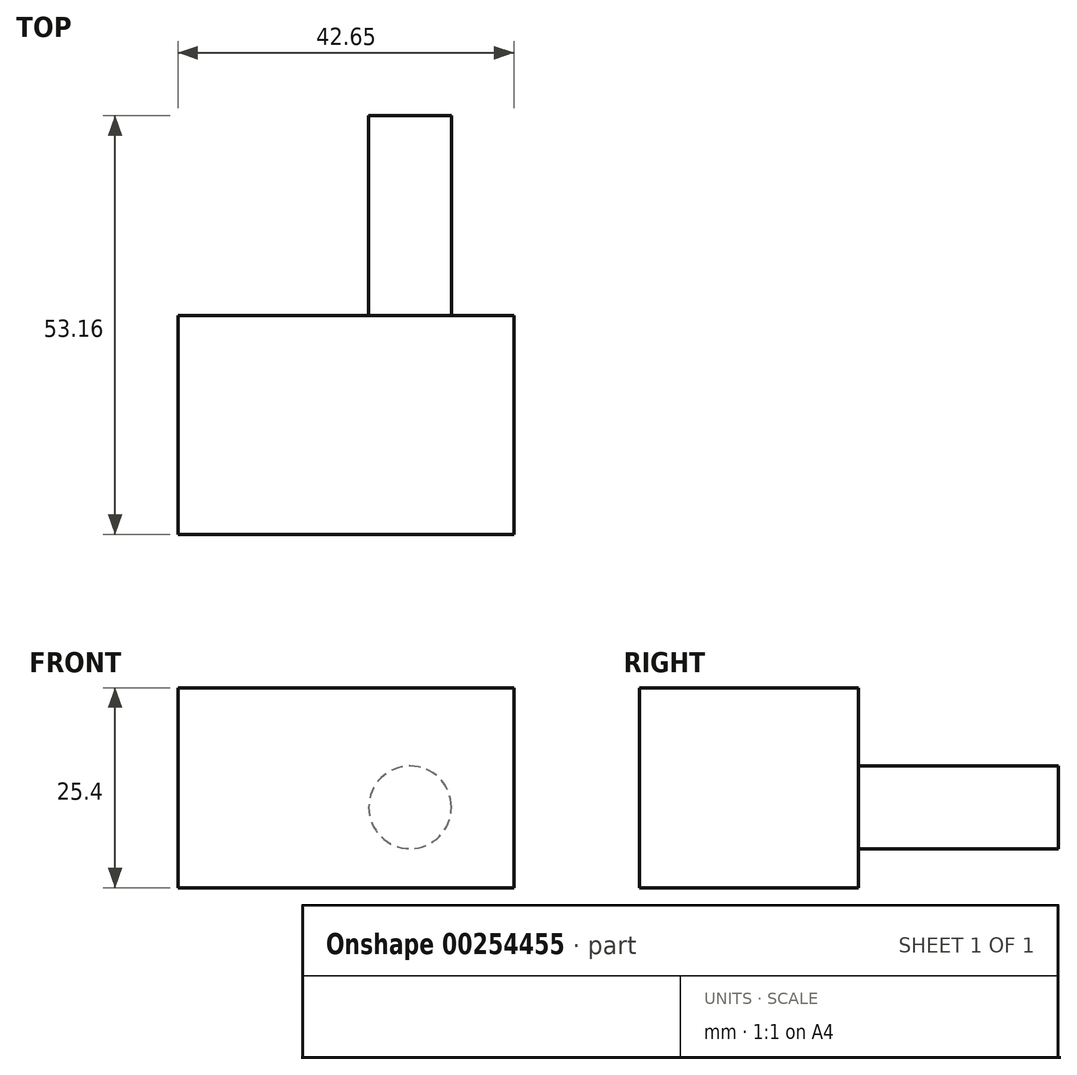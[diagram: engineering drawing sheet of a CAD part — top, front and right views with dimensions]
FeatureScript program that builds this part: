
annotation { "Feature Type Name" : "Feature", "Feature Type Description" : "" }
export const myFeature = defineFeature(function(context is Context, id is Id, definition is map)
    precondition{}
    {
        {
            var Q0;
            Q0=qCreatedBy(makeId("Top.planeOp"),FACE);
            var sketch = newSketch(context, id + "F0", { "sketchPlane" : qUnion([Q0])});
            skLineSegment(sketch, "E0.bottom", {"start": v(-68.58, 17.38) * mm, "end": v(-25.93, 17.38) * mm});
            skLineSegment(sketch, "E0.top", {"start": v(-68.58, -10.38) * mm, "end": v(-25.93, -10.38) * mm});
            skLineSegment(sketch, "E0.left", {"start": v(-68.58, 17.38) * mm, "end": v(-68.58, -10.38) * mm});
            skLineSegment(sketch, "E0.right", {"start": v(-25.93, 17.38) * mm, "end": v(-25.93, -10.38) * mm});
            skSolve(sketch);
        }
        {
            var Q0;
            Q0 = qSketchRegion(id + "F0", true);
            extrude(context, id + "F1", {"entities" : qUnion([Q0]), "depth" : 25.4 * mm});
        }
        {
            var Q0;
            Q0=makeQuery(id+"F1.opExtrude","SWEPT_FACE",FACE,{"disambiguationData":[OSD([sQuery(id+"F0.wireOp",EDGE,"E0.bottom")])]});
            var sketch = newSketch(context, id + "F2", { "sketchPlane" : qUnion([Q0])});
            skCircle(sketch, "E1", {"center": v(39.1, 10.2) * mm, "radius": 5.25 * mm});
            skSolve(sketch);
        }
        {
            var Q0;
            Q0=makeQuery(id+"F2.imprint","IMPRINT",FACE,{"disambiguationData":[TD([[makeQuery(id+"F2.imprint","IMPRINT",EDGE,{"derivedFrom":sQuery(id+"F2.wireOp",EDGE,"E1")}),1.0]])]});
            extrude(context, id + "F3", {"entities" : qUnion([Q0]), "operationType" : NewBodyOperationType.ADD, "depth" : 25.4 * mm});
        }
    });
